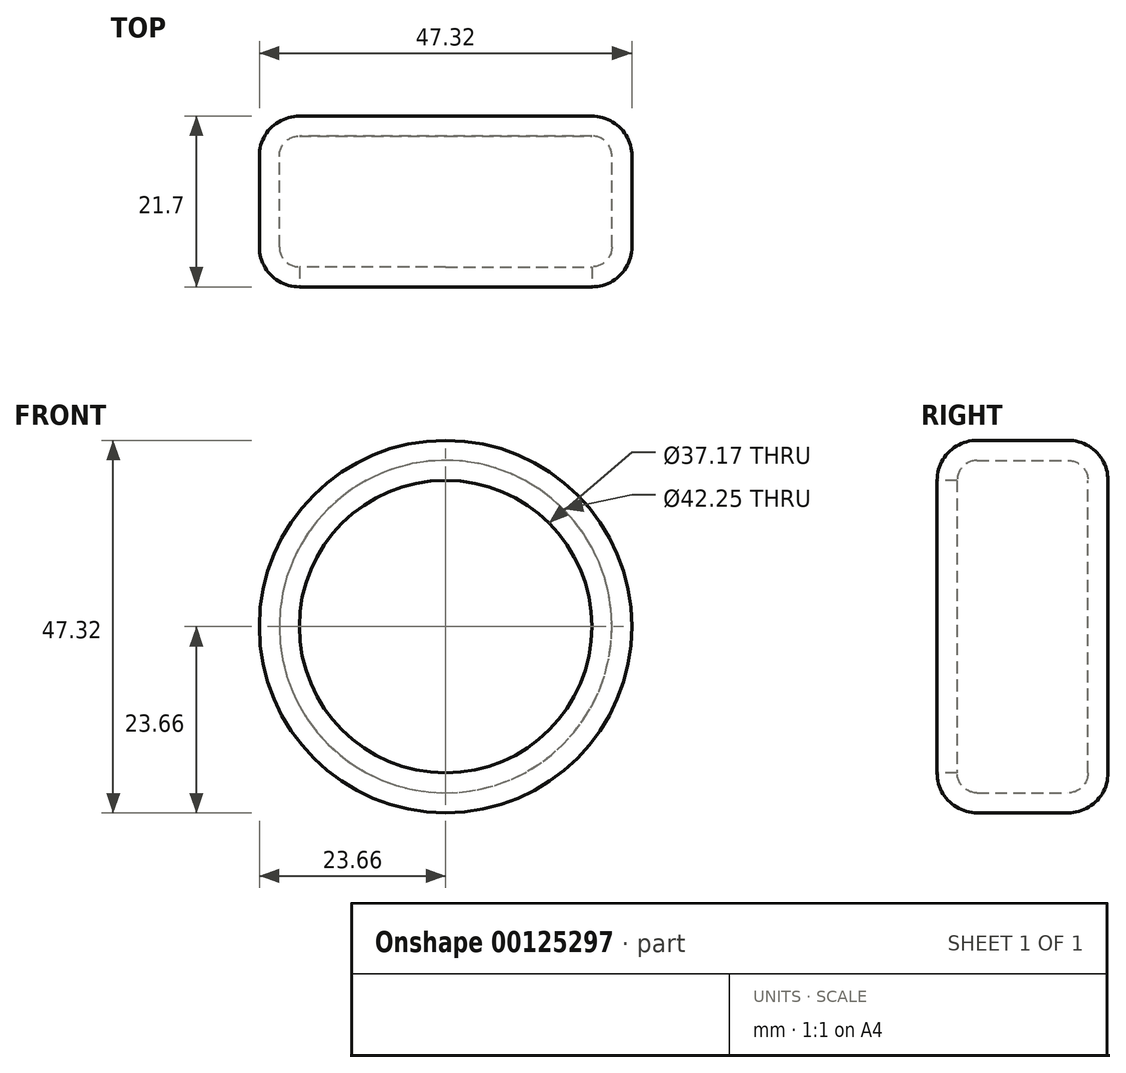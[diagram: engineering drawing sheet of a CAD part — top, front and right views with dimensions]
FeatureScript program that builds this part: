
annotation { "Feature Type Name" : "Feature", "Feature Type Description" : "" }
export const myFeature = defineFeature(function(context is Context, id is Id, definition is map)
    precondition{}
    {
        {
            var Q0;
            Q0=qCreatedBy(makeId("Front.planeOp"),FACE);
            var sketch = newSketch(context, id + "F0", { "sketchPlane" : qUnion([Q0])});
            skCircle(sketch, "E0", {"center": v(0, 0) * mm, "radius": 23.66 * mm});
            skSolve(sketch);
        }
        {
            var Q0;
            Q0=makeQuery(id+"F0.imprint","IMPRINT",FACE,{"disambiguationData":[TD([[makeQuery(id+"F0.imprint","IMPRINT",EDGE,{"derivedFrom":sQuery(id+"F0.wireOp",EDGE,"E0")}),1.0]])]});
            extrude(context, id + "F1", {"entities" : qUnion([Q0]), "depth" : 21.7 * mm});
        }
        {
            var Q0;
            Q0=makeQuery(id+"F1.opExtrude","CAP_EDGE",EDGE,{"disambiguationData":[OSD([sQuery(id+"F0.wireOp",EDGE,"E0")])],"isStart":false});
            var Q1;
            Q1=makeQuery(id+"F1.opExtrude","CAP_EDGE",EDGE,{"disambiguationData":[OSD([sQuery(id+"F0.wireOp",EDGE,"E0")])],"isStart":true});
            fillet(context, id + "F2", {"entities" : qUnion([Q0, Q1]), "radius" : 5.08 * mm, "tangentPropagation" : true, "allowEdgeOverflow" : false});
        }
        {
            var Q0;
            Q0=makeQuery(id+"F1.opExtrude","CAP_FACE",FACE,{"disambiguationData":[OSD([sQuery(id+"F0.wireOp",EDGE,"E0")])],"isStart":false});
            shell(context, id + "F3", {"entities" : qUnion([Q0]), "thickness" : 2.54 * mm});
        }
    });
